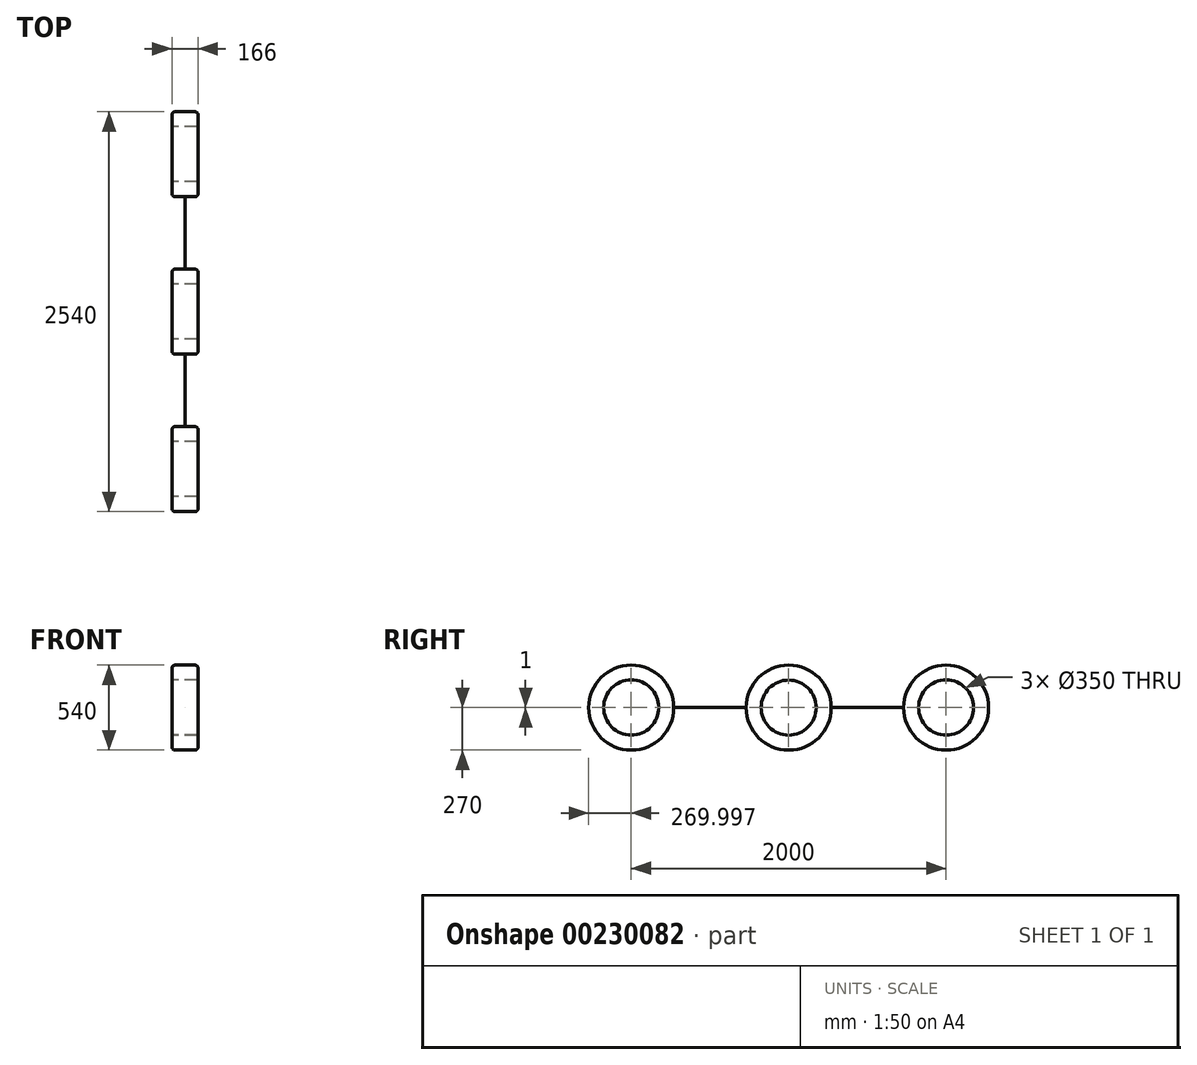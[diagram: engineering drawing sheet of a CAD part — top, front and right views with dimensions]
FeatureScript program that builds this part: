
annotation { "Feature Type Name" : "Feature", "Feature Type Description" : "" }
export const myFeature = defineFeature(function(context is Context, id is Id, definition is map)
    precondition{}
    {
        {
            var Q0;
            Q0=qCreatedBy(makeId("Right.planeOp"),FACE);
            var sketch = newSketch(context, id + "F0", { "sketchPlane" : qUnion([Q0])});
            skCircle(sketch, "E0", {"center": v(-534.92, 0) * mm, "radius": 270 * mm});
            skCircle(sketch, "E1", {"center": v(465.08, 0) * mm, "radius": 270 * mm});
            skCircle(sketch, "E2", {"center": v(1465.08, 0) * mm, "radius": 270 * mm});
            skLineSegment(sketch, "E3.bottom", {"start": v(-534.92, 0) * mm, "end": v(1465.08, 0) * mm});
            skLineSegment(sketch, "E3.top", {"start": v(-534.92, 1) * mm, "end": v(1465.08, 1) * mm});
            skLineSegment(sketch, "E3.left", {"start": v(-534.92, 0) * mm, "end": v(-534.92, 1) * mm});
            skLineSegment(sketch, "E3.right", {"start": v(1465.08, 0) * mm, "end": v(1465.08, 1) * mm});
            skCircle(sketch, "E4", {"center": v(-534.92, 1) * mm, "radius": 175 * mm});
            skCircle(sketch, "E5", {"center": v(465.08, 0) * mm, "radius": 175 * mm});
            skCircle(sketch, "E6", {"center": v(1465.08, 1) * mm, "radius": 175 * mm});
            skSolve(sketch);
        }
        {
            var Q0;
            {var subQ0=sQuery(id+"F0.wireOp",EDGE,"E3.bottom");var subQ1=sQuery(id+"F0.wireOp",EDGE,"E0");var subQ2=makeQuery(id+"F0.imprint","INTERSECT",VERTEX,{"derivedFrom":[subQ1,subQ0]});Q0=makeQuery(id+"F0.imprint","IMPRINT",FACE,{"disambiguationData":[TD([[makeQuery(id+"F0.imprint","IMPRINT",EDGE,{"disambiguationData":[TD([[subQ2,1.0]])],"derivedFrom":subQ1}),1.0]])]});}
            var Q1;
            {var subQ0=sQuery(id+"F0.wireOp",EDGE,"E3.top");var subQ1=sQuery(id+"F0.wireOp",EDGE,"E1");var subQ2=makeQuery(id+"F0.imprint","INTERSECT",VERTEX,{"disambiguationData":[OD(0.0)],"derivedFrom":[subQ1,subQ0]});Q1=makeQuery(id+"F0.imprint","IMPRINT",FACE,{"disambiguationData":[TD([[makeQuery(id+"F0.imprint","IMPRINT",EDGE,{"disambiguationData":[TD([[subQ2,-1.0]])],"derivedFrom":subQ1}),1.0]])]});}
            var Q2;
            {var subQ0=sQuery(id+"F0.wireOp",EDGE,"E3.bottom");var subQ1=sQuery(id+"F0.wireOp",EDGE,"E1");var subQ2=makeQuery(id+"F0.imprint","INTERSECT",VERTEX,{"disambiguationData":[OD(0.0)],"derivedFrom":[subQ1,subQ0]});Q2=makeQuery(id+"F0.imprint","IMPRINT",FACE,{"disambiguationData":[TD([[makeQuery(id+"F0.imprint","IMPRINT",EDGE,{"disambiguationData":[TD([[subQ2,1.0]])],"derivedFrom":subQ1}),1.0]])]});}
            var Q3;
            {var subQ0=sQuery(id+"F0.wireOp",EDGE,"E3.bottom");var subQ1=sQuery(id+"F0.wireOp",EDGE,"E2");var subQ2=makeQuery(id+"F0.imprint","INTERSECT",VERTEX,{"derivedFrom":[subQ1,subQ0]});Q3=makeQuery(id+"F0.imprint","IMPRINT",FACE,{"disambiguationData":[TD([[makeQuery(id+"F0.imprint","IMPRINT",EDGE,{"disambiguationData":[TD([[subQ2,-1.0]])],"derivedFrom":subQ1}),1.0]])]});}
            var Q4;
            {var subQ0=sQuery(id+"F0.wireOp",EDGE,"E3.top");var subQ1=sQuery(id+"F0.wireOp",EDGE,"E1");var subQ2=makeQuery(id+"F0.imprint","INTERSECT",VERTEX,{"disambiguationData":[OD(1.0)],"derivedFrom":[subQ1,subQ0]});Q4=makeQuery(id+"F0.imprint","IMPRINT",FACE,{"disambiguationData":[TD([[makeQuery(id+"F0.imprint","IMPRINT",EDGE,{"disambiguationData":[TD([[subQ2,-1.0]])],"derivedFrom":subQ1}),1.0]])]});}
            var Q5;
            {var subQ0=sQuery(id+"F0.wireOp",EDGE,"E3.top");var subQ1=sQuery(id+"F0.wireOp",EDGE,"E1");var subQ2=makeQuery(id+"F0.imprint","INTERSECT",VERTEX,{"disambiguationData":[OD(0.0)],"derivedFrom":[subQ1,subQ0]});Q5=makeQuery(id+"F0.imprint","IMPRINT",FACE,{"disambiguationData":[TD([[makeQuery(id+"F0.imprint","IMPRINT",EDGE,{"disambiguationData":[TD([[subQ2,1.0]])],"derivedFrom":subQ1}),1.0]])]});}
            var Q6;
            {var subQ0=sQuery(id+"F0.wireOp",EDGE,"E3.bottom");var subQ1=sQuery(id+"F0.wireOp",EDGE,"E2");var subQ2=makeQuery(id+"F0.imprint","INTERSECT",VERTEX,{"derivedFrom":[subQ1,subQ0]});Q6=makeQuery(id+"F0.imprint","IMPRINT",FACE,{"disambiguationData":[TD([[makeQuery(id+"F0.imprint","IMPRINT",EDGE,{"disambiguationData":[TD([[subQ2,1.0]])],"derivedFrom":subQ1}),1.0]])]});}
            var Q7;
            {var subQ0=sQuery(id+"F0.wireOp",EDGE,"E3.bottom");var subQ1=sQuery(id+"F0.wireOp",EDGE,"E0");var subQ2=makeQuery(id+"F0.imprint","INTERSECT",VERTEX,{"derivedFrom":[subQ1,subQ0]});Q7=makeQuery(id+"F0.imprint","IMPRINT",FACE,{"disambiguationData":[TD([[makeQuery(id+"F0.imprint","IMPRINT",EDGE,{"disambiguationData":[TD([[subQ2,-1.0]])],"derivedFrom":subQ1}),1.0]])]});}
            extrude(context, id + "F1", {"entities" : qUnion([Q0, Q1, Q2, Q3, Q4, Q5, Q6, Q7]), "endBound" : BoundingType.SYMMETRIC, "depth" : 166 * mm});
        }
        {
            var Q0;
            Q0=makeQuery(id+"F1.opExtrude","CAP_EDGE",EDGE,{"disambiguationData":[OSD([sQuery(id+"F0.wireOp",EDGE,"E0")])],"isStart":false});
            var Q1;
            Q1=makeQuery(id+"F1.opExtrude","CAP_EDGE",EDGE,{"disambiguationData":[OSD([sQuery(id+"F0.wireOp",EDGE,"E0")])],"isStart":true});
            var Q2;
            {var subQ0=sQuery(id+"F0.wireOp",EDGE,"E3.top");var subQ1=sQuery(id+"F0.wireOp",EDGE,"E1");Q2=makeQuery(id+"F1.opExtrude","CAP_EDGE",EDGE,{"disambiguationData":[OSD([subQ1]),TDD([makeQuery(id+"F0.imprint","IMPRINT",EDGE,{"disambiguationData":[TD([[makeQuery(id+"F0.imprint","INTERSECT",VERTEX,{"disambiguationData":[OD(0.0)],"derivedFrom":[subQ1,subQ0]}),-1.0]])],"derivedFrom":subQ1})])],"isStart":false});}
            var Q3;
            {var subQ0=sQuery(id+"F0.wireOp",EDGE,"E3.top");var subQ1=sQuery(id+"F0.wireOp",EDGE,"E1");Q3=makeQuery(id+"F1.opExtrude","CAP_EDGE",EDGE,{"disambiguationData":[OSD([subQ1]),TDD([makeQuery(id+"F0.imprint","IMPRINT",EDGE,{"disambiguationData":[TD([[makeQuery(id+"F0.imprint","INTERSECT",VERTEX,{"disambiguationData":[OD(0.0)],"derivedFrom":[subQ1,subQ0]}),-1.0]])],"derivedFrom":subQ1})])],"isStart":true});}
            var Q4;
            {var subQ0=sQuery(id+"F0.wireOp",EDGE,"E3.bottom");var subQ1=sQuery(id+"F0.wireOp",EDGE,"E1");Q4=makeQuery(id+"F1.opExtrude","CAP_EDGE",EDGE,{"disambiguationData":[OSD([subQ1]),TDD([makeQuery(id+"F0.imprint","IMPRINT",EDGE,{"disambiguationData":[TD([[makeQuery(id+"F0.imprint","INTERSECT",VERTEX,{"disambiguationData":[OD(0.0)],"derivedFrom":[subQ1,subQ0]}),1.0]])],"derivedFrom":subQ1})])],"isStart":false});}
            var Q5;
            Q5=makeQuery(id+"F1.opExtrude","CAP_EDGE",EDGE,{"disambiguationData":[OSD([sQuery(id+"F0.wireOp",EDGE,"E2")])],"isStart":false});
            var Q6;
            Q6=makeQuery(id+"F1.opExtrude","CAP_EDGE",EDGE,{"disambiguationData":[OSD([sQuery(id+"F0.wireOp",EDGE,"E2")])],"isStart":true});
            var Q7;
            {var subQ0=sQuery(id+"F0.wireOp",EDGE,"E3.bottom");var subQ1=sQuery(id+"F0.wireOp",EDGE,"E1");Q7=makeQuery(id+"F1.opExtrude","CAP_EDGE",EDGE,{"disambiguationData":[OSD([subQ1]),TDD([makeQuery(id+"F0.imprint","IMPRINT",EDGE,{"disambiguationData":[TD([[makeQuery(id+"F0.imprint","INTERSECT",VERTEX,{"disambiguationData":[OD(0.0)],"derivedFrom":[subQ1,subQ0]}),1.0]])],"derivedFrom":subQ1})])],"isStart":true});}
            fillet(context, id + "F2", {"entities" : qUnion([Q0, Q1, Q2, Q3, Q4, Q5, Q6, Q7]), "radius" : 20 * mm, "tangentPropagation" : true, "allowEdgeOverflow" : false});
        }
        {
            var Q0;
            Q0 = qSketchRegion(id + "F0", true);
            extrude(context, id + "F3", {"entities" : qUnion([Q0]), "operationType" : NewBodyOperationType.ADD, "endBound" : BoundingType.SYMMETRIC, "depth" : 1 * mm});
        }
        {
            var Q0;
            Q0=makeQuery(id+"F1.opExtrude","CAP_EDGE",EDGE,{"disambiguationData":[OSD([sQuery(id+"F0.wireOp",EDGE,"E4")])],"isStart":false});
            var Q1;
            Q1=makeQuery(id+"F1.opExtrude","CAP_EDGE",EDGE,{"disambiguationData":[OSD([sQuery(id+"F0.wireOp",EDGE,"E4")])],"isStart":true});
            var Q2;
            Q2=makeQuery(id+"F1.opExtrude","CAP_EDGE",EDGE,{"disambiguationData":[OSD([sQuery(id+"F0.wireOp",EDGE,"E5")])],"isStart":false});
            var Q3;
            Q3=makeQuery(id+"F1.opExtrude","CAP_EDGE",EDGE,{"disambiguationData":[OSD([sQuery(id+"F0.wireOp",EDGE,"E5")])],"isStart":true});
            var Q4;
            Q4=makeQuery(id+"F1.opExtrude","CAP_EDGE",EDGE,{"disambiguationData":[OSD([sQuery(id+"F0.wireOp",EDGE,"E6")])],"isStart":false});
            var Q5;
            Q5=makeQuery(id+"F1.opExtrude","CAP_EDGE",EDGE,{"disambiguationData":[OSD([sQuery(id+"F0.wireOp",EDGE,"E6")])],"isStart":true});
            fillet(context, id + "F4", {"entities" : qUnion([Q0, Q1, Q2, Q3, Q4, Q5]), "radius" : 10 * mm, "tangentPropagation" : true, "allowEdgeOverflow" : false});
        }
    });
